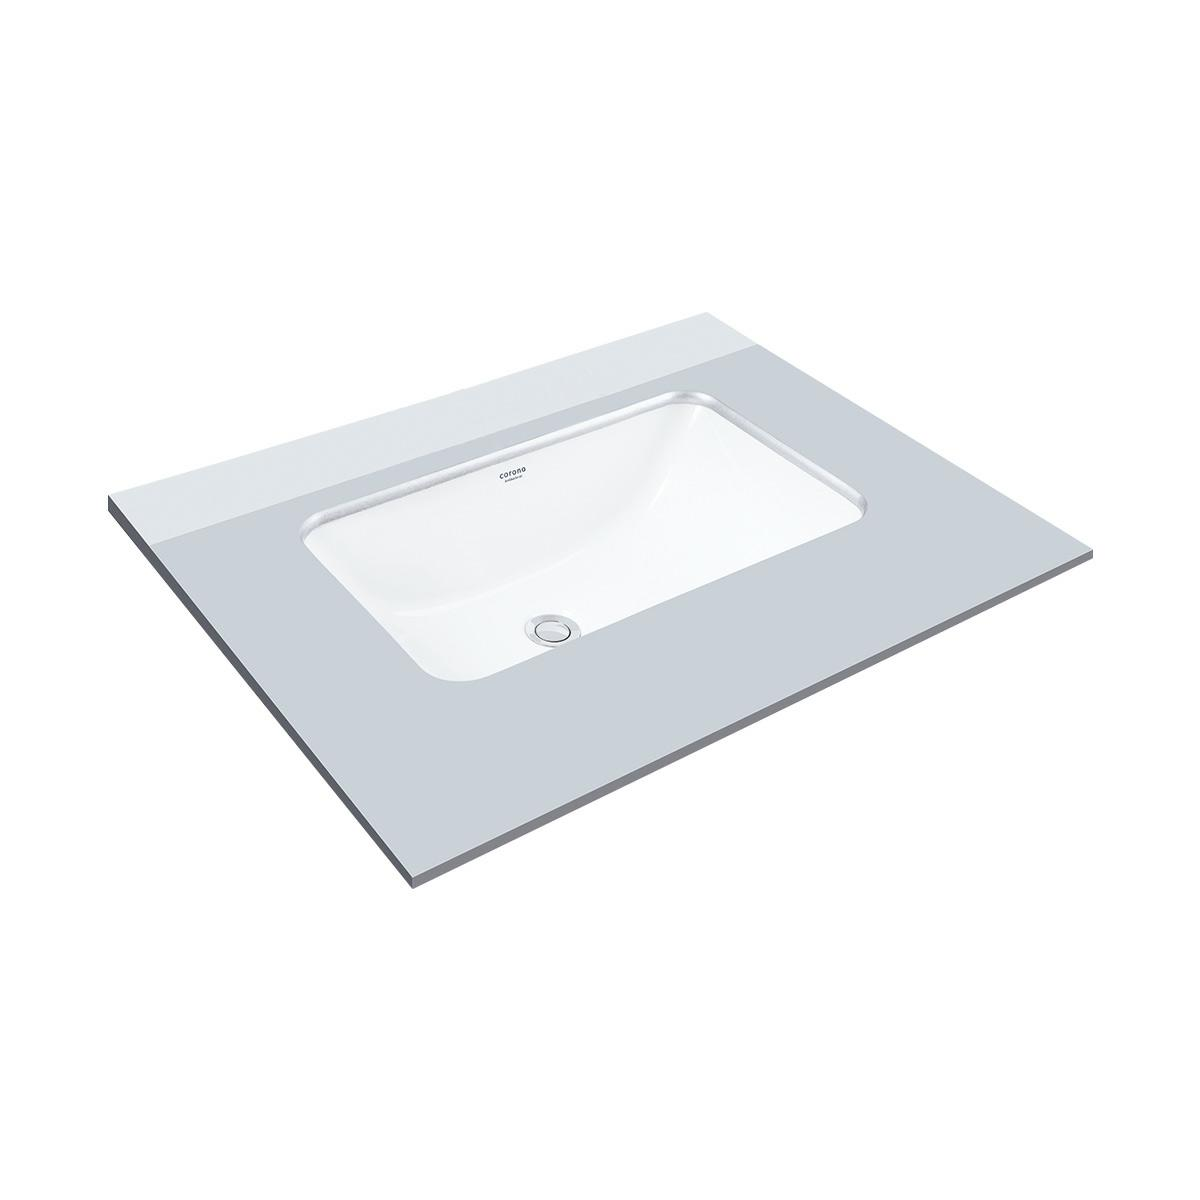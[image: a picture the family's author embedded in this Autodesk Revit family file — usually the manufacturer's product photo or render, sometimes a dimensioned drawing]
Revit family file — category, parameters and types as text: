
# Revit family: CCMX-CORONA_NOVARA
name_source: partatom
category: Plumbing Fixtures
units: mm (PartAtom-declared; Revit-internal decimal feet)

## family parameters
Always vertical = Yes
Cut with Voids When Loaded = No
OmniClass Number = 23.45.00.00
OmniClass Title = Sanitary, Laundry, and Cleaning Equipment
Part Type = Normal
Room Calculation Point = No
Round Connector Dimension = Use Diameter
Shared = No
Work Plane-Based = No

## types (1)
- CCMX-CORONA_NOVARA
    Assembly Code = D2010.60
    Description = * Las fotografías de productos y ambientes son ilustrativas, algunos atributos pueden variar de acuerdo a la resolución de tu pantalla.

Lavamanos bajo cubierta en porcelana sanitaria. Diseño contemporáneo inspirado en formas clásicas. Cuenta con agujero integral de drenaje que evita el rebose.
    Dimensiones = https://coronamexico.com
    Garantia de Producto = 20 años en porcelana sanitaria
    Keynote = 224116
    Manufacturer = CORONA
    Model = Novara
    Type Image = Novara_.jpg
    URL = https://coronamexico.com

## geometry (parser evidence)
native form markers: Sweep x3
no freeform markers — native parametric forms only
